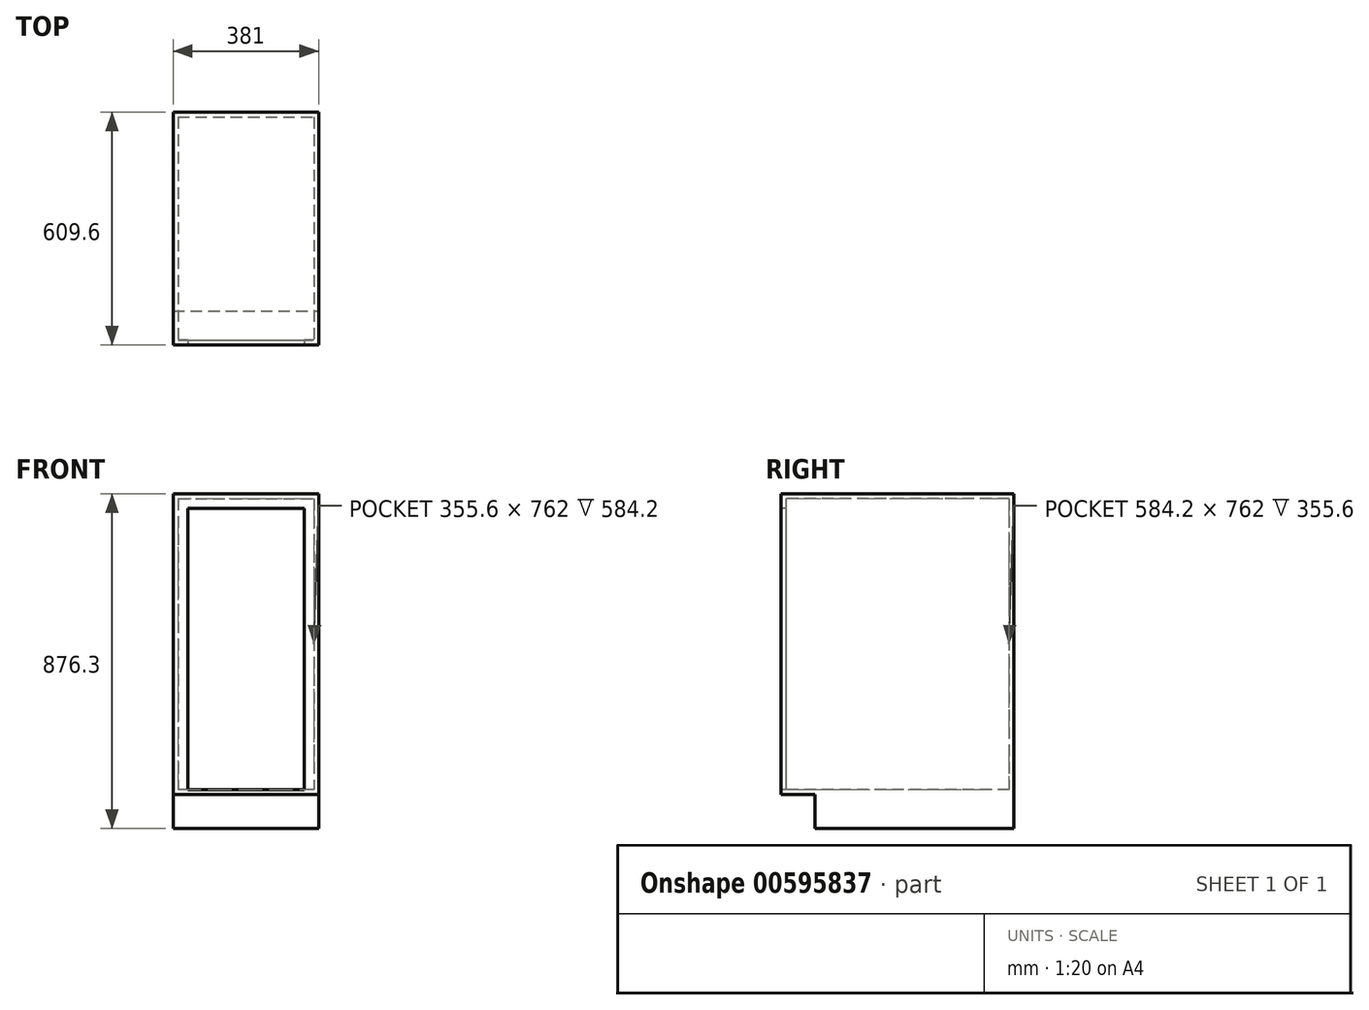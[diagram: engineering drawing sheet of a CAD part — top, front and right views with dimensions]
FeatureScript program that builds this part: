
annotation { "Feature Type Name" : "Feature", "Feature Type Description" : "" }
export const myFeature = defineFeature(function(context is Context, id is Id, definition is map)
    precondition{}
    {
        {
            var Q0;
            Q0=qCreatedBy(makeId("Top.planeOp"),FACE);
            var sketch = newSketch(context, id + "F0", { "sketchPlane" : qUnion([Q0])});
            skLineSegment(sketch, "E0.bottom", {"start": v(0, 0) * mm, "end": v(381, 0) * mm});
            skLineSegment(sketch, "E0.top", {"start": v(0, -609.6) * mm, "end": v(381, -609.6) * mm});
            skLineSegment(sketch, "E0.left", {"start": v(0, 0) * mm, "end": v(0, -609.6) * mm});
            skLineSegment(sketch, "E0.right", {"start": v(381, 0) * mm, "end": v(381, -609.6) * mm});
            skSolve(sketch);
        }
        {
            var Q0;
            Q0=qSketchRegion(id+"F0",true);
            extrude(context, id + "F1", {"entities" : qUnion([Q0]), "depth" : 876.3 * mm, "offsetDistance" : 25.4 * mm});
        }
        {
            var Q0;
            Q0=makeQuery(id+"F1.opExtrude","SWEPT_FACE",FACE,{"disambiguationData":[OSD([sQuery(id+"F0.wireOp",EDGE,"E0.top")])]});
            var sketch = newSketch(context, id + "F2", { "sketchPlane" : qUnion([Q0])});
            skLineSegment(sketch, "E1.bottom", {"start": v(0, 0) * mm, "end": v(381, 0) * mm});
            skLineSegment(sketch, "E1.top", {"start": v(0, 88.9) * mm, "end": v(381, 88.9) * mm});
            skLineSegment(sketch, "E1.left", {"start": v(0, 0) * mm, "end": v(0, 88.9) * mm});
            skLineSegment(sketch, "E1.right", {"start": v(381, 0) * mm, "end": v(381, 88.9) * mm});
            skSolve(sketch);
        }
        {
            var Q0;
            Q0=qSketchRegion(id+"F2",true);
            extrude(context, id + "F3", {"entities" : qUnion([Q0]), "operationType" : NewBodyOperationType.REMOVE, "oppositeDirection" : true, "depth" : 88.9 * mm, "offsetDistance" : 25.4 * mm});
        }
        {
            var Q0;
            Q0=makeQuery(id+"F1.opExtrude","SWEPT_FACE",FACE,{"disambiguationData":[OSD([sQuery(id+"F0.wireOp",EDGE,"E0.top")])]});
            shell(context, id + "F4", {"entities" : qUnion([Q0]), "thickness" : 12.7 * mm});
        }
        {
            var Q0;
            {var subQ0=sQuery(id+"F0.wireOp",EDGE,"E0.right");var subQ1=sQuery(id+"F0.wireOp",EDGE,"E0.left");var subQ2=sQuery(id+"F0.wireOp",EDGE,"E0.top");var subQ3=sQuery(id+"F0.wireOp",EDGE,"E0.bottom");Q0=makeQuery(id+"F4.opShell","OFFSET_FACE",FACE,{"disambiguationData":[OSD([subQ3,subQ2,subQ1,subQ0]),TDD([makeQuery(id+"F1.opExtrude","CAP_FACE",FACE,{"disambiguationData":[OSD([subQ3,subQ2,subQ1,subQ0])],"isStart":true})])]});}
            var Q1;
            Q1=makeQuery(id+"F4.opShell","OFFSET_FACE",FACE,{"disambiguationData":[OSD([sQuery(id+"F2.wireOp",EDGE,"E1.top")])]});
            extrude(context, id + "F5", {"entities" : qUnion([Q0]), "operationType" : NewBodyOperationType.ADD, "endBound" : BoundingType.UP_TO_SURFACE, "depth" : 25.4 * mm, "endBoundEntityFace" : qUnion([Q1]), "offsetDistance" : 25.4 * mm});
        }
        {
            var Q0;
            Q0=makeQuery(id+"F1.opExtrude","SWEPT_FACE",FACE,{"disambiguationData":[OSD([sQuery(id+"F0.wireOp",EDGE,"E0.top")])]});
            var sketch = newSketch(context, id + "F6", { "sketchPlane" : qUnion([Q0])});
            skLineSegment(sketch, "E2.0", {"start": v(38.1, 838.2) * mm, "end": v(342.9, 838.2) * mm});
            skLineSegment(sketch, "E2.1", {"start": v(38.1, 838.2) * mm, "end": v(38.1, 101.6) * mm});
            skLineSegment(sketch, "E2.3", {"start": v(342.9, 838.2) * mm, "end": v(342.9, 101.6) * mm});
            skSolve(sketch);
        }
        {
            var Q0;
            Q0=makeQuery(id+"F6.imprint","IMPRINT",FACE,{"disambiguationData":[TD([[makeQuery(id+"F6.imprint","IMPRINT",EDGE,{"derivedFrom":sQuery(id+"F6.wireOp",EDGE,"E2.0")}),1.0]])]});
            var Q1;
            {var subQ1=sQuery(id+"F0.wireOp",EDGE,"E0.top");Q1=makeQuery(id+"F6.imprint","IMPRINT",FACE,{"disambiguationData":[TD([[makeQuery(id+"F6.imprint","IMPRINT",EDGE,{"derivedFrom":makeQuery(id+"F1.opExtrude","CAP_EDGE",EDGE,{"disambiguationData":[OSD([subQ1])],"isStart":false})}),-1.0]])]});}
            extrude(context, id + "F7", {"entities" : qUnion([Q0, Q1]), "operationType" : NewBodyOperationType.ADD, "oppositeDirection" : true, "depth" : 12.7 * mm, "offsetDistance" : 25.4 * mm});
        }
    });
